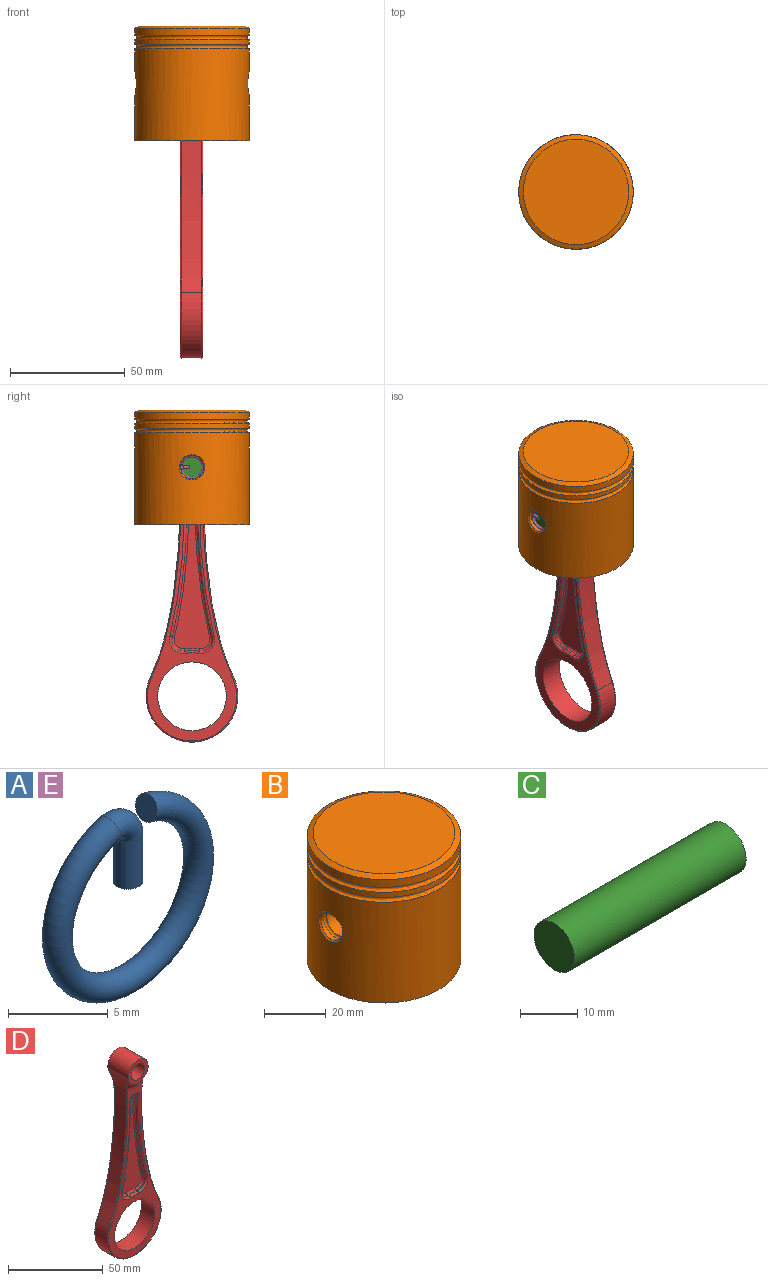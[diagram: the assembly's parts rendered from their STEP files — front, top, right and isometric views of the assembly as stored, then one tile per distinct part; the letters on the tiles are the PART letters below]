
ASSEMBLY  parts=5 mates=4
PART A: 5 faces, bbox 12.4x1.5x12.3 mm
  f0: plane 1.5x1.5mm, normal (0,0,-1), area 1.8mm2, adj f2
  f1: plane 1.5x1.45mm, normal (-0.97,0,0.26), area 1.8mm2, adj f4
  f2: cylinder r=0.75mm len=2.87mm, axis (0,0,1), area 13.5mm2, adj f0,f3
  f3: torus R=1mm, axis (0,-1,0), area 8.6mm2, adj f2,f4
  f4: torus R=5mm, axis (0,-1,0), area 135.9mm2, adj f1,f3
PART B: 22 faces, bbox 55.7x55.7x50 mm
  f0: cylinder r=5mm len=10mm, axis (1,0,0), area 55mm2, adj f19,f21
  f1: cylinder r=5mm len=10mm, axis (1,0,0), area 274.9mm2, adj f15,f18
  f2: cylinder r=5mm len=10mm, axis (1,0,0), area 55mm2, adj f18,f20
  f3: cylinder r=6.5mm len=13mm, axis (-1,0,0), area 388mm2, adj f12,f16
  f4: cylinder r=25mm len=50mm, axis (0,0,-1), area 471.2mm2, adj f6,f7
  f5: plane 46x46mm, normal (0,0,1), area 1661.9mm2, adj f6
  f6: cone r=23mm half-angle=63.4deg, axis (0,0,-1), area 337.2mm2, adj f4,f5
  f7: torus R=25mm, axis (0,0,-1), area 480.9mm2, adj f4,f8
  f8: cylinder r=25mm len=50mm, axis (0,0,-1), area 314.2mm2, adj f7,f9
  f9: torus R=25mm, axis (0,0,-1), area 480.9mm2, adj f8,f11
  f10: plane 50x50mm, normal (0,0,-1), area 443mm2, adj f11,f12
  f11: cylinder r=25mm len=50mm, axis (0,0,-1), area 6088.1mm2, adj f9,f10,f20,f21
  f12: cylinder r=22mm len=44mm, axis (0,0,-1), area 4569.4mm2, adj f3,f10,f13,f14
  f13: plane 44x44mm, normal (0,0,-1), area 1520.5mm2, adj f12
  f14: cylinder r=6.5mm len=13mm, axis (-1,0,0), area 388mm2, adj f12,f15
  f15: plane 13x13mm, normal (-1,0,0), area 54.2mm2, adj f1,f14
  f16: plane 13x13mm, normal (1,0,0), area 54.2mm2, adj f3,f17
  f17: cylinder r=5mm len=10mm, axis (1,0,0), area 274.9mm2, adj f16,f19
  f18: torus R=5mm, axis (-1,0,0), area 81.1mm2, adj f1,f2
  f19: torus R=5mm, axis (-1,0,0), area 81.1mm2, adj f0,f17
  f20: bspline ~11.22x11mm, area 24.8mm2, adj f2,f11
  f21: bspline ~11.22x11mm, area 24.8mm2, adj f0,f11
PART C: 3 faces, bbox 42.5x10x10 mm
  f0: cylinder r=5mm len=42.5mm, axis (-1,0,0), area 1335.2mm2, adj f1,f2
  f1: plane 10x10mm, normal (1,0,0), area 78.5mm2, adj f0
  f2: plane 10x10mm, normal (-1,0,0), area 78.5mm2, adj f0
PART D: 66 faces, bbox 50.9x20.2x129.4 mm
  f0: cylinder r=20mm len=40mm, axis (0,1,0), area 725.3mm2, adj f1,f3,f33,f63
  f1: extruded ~89.85x14.74mm, area 850.1mm2, adj f0,f2,f31,f32,f61,f62
  f2: cylinder r=7.5mm len=15mm, axis (0,1,0), area 400.3mm2, adj f1,f3,f7,f31,f35,f37,f61,f65
  f3: extruded ~89.85x14.74mm, area 850.1mm2, adj f0,f2,f34,f35,f64,f65
  f4: plane 109.04x39mm, normal (0,-1,0), area 802.4mm2, adj f5,f8,f18,f19,f20,f21,f22,f23
  f5: cylinder r=15mm len=30mm, axis (0,-1,0), area 942.5mm2, adj f4,f36
  f6: cylinder r=5mm len=15mm, axis (0,-1,0), area 471.2mm2, adj f7,f37
  f7: plane 15.23x15.23mm, normal (0,-1,0), area 98.1mm2, adj f2,f6,f8,f31,f35
  f8: torus R=11.83mm, axis (0,-1,0), area 81.8mm2, adj f4,f7,f31,f35
  f9: cylinder r=5mm len=6.26mm, axis (0,-1,0), area 9.9mm2, adj f10,f16,f19,f27
  f10: extruded ~56.18x6.24mm, area 56.7mm2, adj f9,f11,f21,f26
  f11: cylinder r=1mm len=2mm, axis (0,-1,0), area 2.6mm2, adj f10,f12,f17,f23,f26
  f12: plane 3.05x2mm, normal (0,0,-1), area 6.1mm2, adj f11,f13,f17,f25
  f13: cylinder r=1mm len=2mm, axis (0,-1,0), area 2.6mm2, adj f12,f14,f17,f24,f30
  f14: extruded ~56.18x6.24mm, area 56.7mm2, adj f13,f15,f22,f30
  f15: cylinder r=5mm len=6.26mm, axis (0,-1,0), area 9.9mm2, adj f14,f16,f20,f29
  f16: cylinder r=20mm len=6.17mm, axis (0,-1,0), area 6.2mm2, adj f9,f15,f18,f28
  f17: plane 62.48x15.71mm, normal (0,-1,0), area 457.2mm2, adj f11,f12,f13,f26,f27,f28,f29,f30
  f18: torus R=19mm, axis (0,-1,0), area 9.6mm2, adj f4,f16,f19,f20
  f19: torus R=6mm, axis (0,-1,0), area 16.7mm2, adj f4,f9,f18,f21
  f20: torus R=6mm, axis (0,-1,0), area 16.7mm2, adj f4,f15,f18,f22
  f21: bspline ~75.6x11.02mm, area 88.9mm2, adj f4,f10,f19,f23
  f22: bspline ~75.6x11.02mm, area 88.9mm2, adj f4,f14,f20,f24
  f23: torus R=2mm, axis (0,-1,0), area 3.4mm2, adj f4,f11,f21,f25
  f24: torus R=2mm, axis (0,-1,0), area 3.4mm2, adj f4,f13,f22,f25
  f25: cylinder r=1mm len=3.05mm, axis (-1,0,0), area 4.8mm2, adj f4,f12,f23,f24
  f26: bspline ~71.72x11.02mm, area 90mm2, adj f10,f11,f17,f27
  f27: torus R=4mm, axis (0,-1,0), area 14.4mm2, adj f9,f17,f26,f28
  f28: torus R=21mm, axis (0,-1,0), area 9.9mm2, adj f16,f17,f27,f29
  f29: torus R=4mm, axis (0,-1,0), area 14.4mm2, adj f15,f17,f28,f30
  f30: bspline ~71.74x11.02mm, area 90mm2, adj f13,f14,f17,f29
  f31: bspline ~12.12x3.11mm, area 5mm2, adj f1,f2,f7,f8,f32
  f32: bspline ~89.19x14.92mm, area 64.9mm2, adj f1,f4,f31,f33
  f33: torus R=19.5mm, axis (0,-1,0), area 62.7mm2, adj f0,f4,f32,f34
  f34: bspline ~100.65x20.38mm, area 64.9mm2, adj f3,f4,f33,f35
  f35: bspline ~12.12x3.11mm, area 5mm2, adj f2,f3,f7,f8,f34
  f36: plane 109.03x39mm, normal (0,1,0), area 802.4mm2, adj f5,f38,f48,f49,f50,f51,f52,f53
  f37: plane 15.23x15.23mm, normal (0,1,0), area 98.1mm2, adj f2,f6,f38,f61,f65
  f38: torus R=11.83mm, axis (0,1,0), area 81.8mm2, adj f36,f37,f61,f65
  f39: cylinder r=5mm len=6.26mm, axis (0,1,0), area 9.9mm2, adj f40,f46,f49,f57
  f40: extruded ~56.18x6.24mm, area 56.7mm2, adj f39,f41,f51,f56
  f41: cylinder r=1mm len=2mm, axis (0,1,0), area 2.6mm2, adj f40,f42,f47,f53,f56
  f42: plane 3.05x2mm, normal (0,0,-1), area 6.1mm2, adj f41,f43,f47,f55
  f43: cylinder r=1mm len=2mm, axis (0,1,0), area 2.6mm2, adj f42,f44,f47,f54,f60
  f44: extruded ~56.18x6.24mm, area 56.7mm2, adj f43,f45,f52,f60
  f45: cylinder r=5mm len=6.26mm, axis (0,1,0), area 9.9mm2, adj f44,f46,f50,f59
  f46: cylinder r=20mm len=6.17mm, axis (0,1,0), area 6.2mm2, adj f39,f45,f48,f58
  f47: plane 62.48x15.71mm, normal (0,1,0), area 457.2mm2, adj f41,f42,f43,f56,f57,f58,f59,f60
  f48: torus R=19mm, axis (0,1,0), area 9.6mm2, adj f36,f46,f49,f50
  f49: torus R=6mm, axis (0,1,0), area 16.7mm2, adj f36,f39,f48,f51
  f50: torus R=6mm, axis (0,1,0), area 16.7mm2, adj f36,f45,f48,f52
  f51: bspline ~75.6x11.02mm, area 88.9mm2, adj f36,f40,f49,f53
  f52: bspline ~75.6x11.02mm, area 88.9mm2, adj f36,f44,f50,f54
  f53: torus R=2mm, axis (0,1,0), area 3.4mm2, adj f36,f41,f51,f55
  f54: torus R=2mm, axis (0,1,0), area 3.4mm2, adj f36,f43,f52,f55
  f55: cylinder r=1mm len=3.05mm, axis (-1,0,0), area 4.8mm2, adj f36,f42,f53,f54
  f56: bspline ~71.72x11.02mm, area 90mm2, adj f40,f41,f47,f57
  f57: torus R=4mm, axis (0,1,0), area 14.4mm2, adj f39,f47,f56,f58
  f58: torus R=21mm, axis (0,1,0), area 9.9mm2, adj f46,f47,f57,f59
  f59: torus R=4mm, axis (0,1,0), area 14.4mm2, adj f45,f47,f58,f60
  f60: bspline ~71.74x11.02mm, area 90mm2, adj f43,f44,f47,f59
  f61: bspline ~12.12x3.11mm, area 5mm2, adj f1,f2,f37,f38,f62
  f62: bspline ~100.65x20.38mm, area 64.9mm2, adj f1,f36,f61,f63
  f63: torus R=19.5mm, axis (0,1,0), area 62.7mm2, adj f0,f36,f62,f64
  f64: bspline ~100.65x20.38mm, area 64.9mm2, adj f3,f36,f63,f65
  f65: bspline ~12.12x3.11mm, area 5mm2, adj f2,f3,f37,f38,f64
PART E: same geometry as A
PLACE A rot(axis=(0,0,-1),90deg) t=(-0.88,-16.7,-15.17)mm
PLACE B t=(-22.88,-16.7,-40.17)mm
PLACE C t=(-22.85,-16.7,-15.17)mm
PLACE D rot(axis=(0,0,-1),90deg) t=(-23.1,-16.7,-115.17)mm
PLACE E rot(axis=(-0.58,-0.58,-0.58),120deg) t=(-44.88,-16.7,-15.17)mm
MATE slider D.f2 <-> C.f0  axis (-1,0,0) through (-15.6,-16.7,-15.17)mm
MATE fastened A.f4 <-> B.f18  axis (-1,0,0) through (-0.88,-16.7,-15.17)mm
MATE slider C.f0 <-> B.f0  axis (-1,0,0) through (-1.6,-16.7,-15.17)mm
MATE fastened E.f4 <-> B.f18  axis (-1,0,0) through (-44.88,-16.7,-15.17)mm
